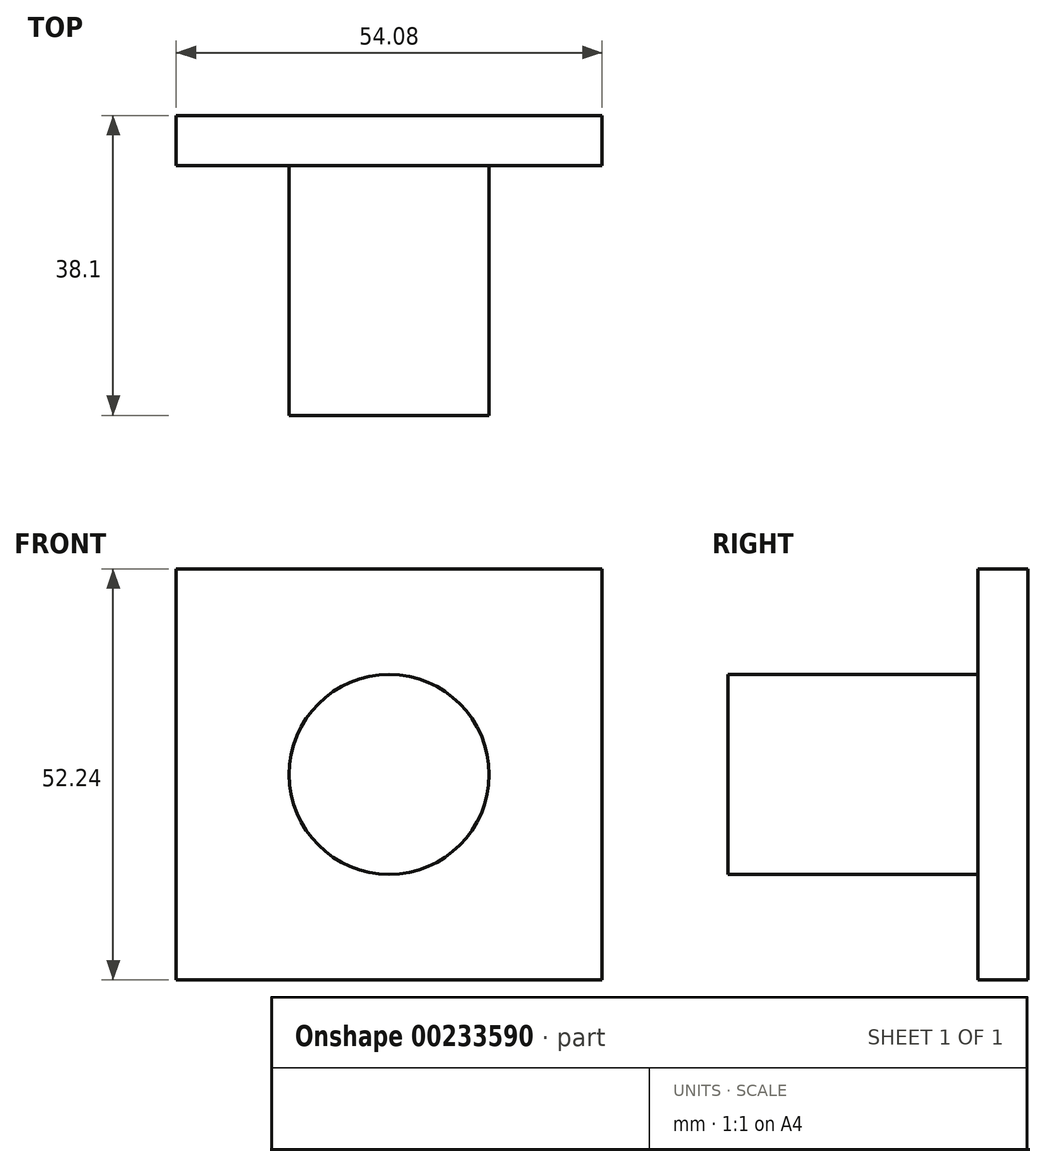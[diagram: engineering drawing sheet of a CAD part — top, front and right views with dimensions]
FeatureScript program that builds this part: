
annotation { "Feature Type Name" : "Feature", "Feature Type Description" : "" }
export const myFeature = defineFeature(function(context is Context, id is Id, definition is map)
    precondition{}
    {
        {
            var Q0;
            Q0=qCreatedBy(makeId("Front.planeOp"),FACE);
            var sketch = newSketch(context, id + "F0", { "sketchPlane" : qUnion([Q0])});
            skLineSegment(sketch, "E0.bottom", {"start": v(27.04, -26.12) * mm, "end": v(-27.04, -26.12) * mm});
            skLineSegment(sketch, "E0.top", {"start": v(27.04, 26.12) * mm, "end": v(-27.04, 26.12) * mm});
            skLineSegment(sketch, "E0.left", {"start": v(27.04, -26.12) * mm, "end": v(27.04, 26.12) * mm});
            skLineSegment(sketch, "E0.right", {"start": v(-27.04, -26.12) * mm, "end": v(-27.04, 26.12) * mm});
            skPoint(sketch, "E0.middle", {"position": v(0, 0) * mm});
            skCircle(sketch, "E1", {"center": v(0, 0) * mm, "radius": 12.7 * mm});
            skSolve(sketch);
        }
        {
            var Q0;
            Q0=makeQuery(id+"F0.imprint","IMPRINT",FACE,{"disambiguationData":[TD([[makeQuery(id+"F0.imprint","IMPRINT",EDGE,{"derivedFrom":sQuery(id+"F0.wireOp",EDGE,"E1")}),1.0]])]});
            extrude(context, id + "F1", {"entities" : qUnion([Q0]), "depth" : 38.1 * mm});
        }
        {
            var Q0;
            Q0=makeQuery(id+"F0.imprint","IMPRINT",FACE,{"disambiguationData":[TD([[makeQuery(id+"F0.imprint","IMPRINT",EDGE,{"derivedFrom":sQuery(id+"F0.wireOp",EDGE,"E0.bottom")}),-1.0]])]});
            extrude(context, id + "F2", {"entities" : qUnion([Q0]), "operationType" : NewBodyOperationType.ADD, "depth" : 6.35 * mm});
        }
    });
